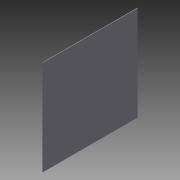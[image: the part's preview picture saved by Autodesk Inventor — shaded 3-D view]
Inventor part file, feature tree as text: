
AUTODESK INVENTOR PART (.ipt)
format: ipt  version: 2013 (Build 170138000, 138)  size: 72,704 bytes
history: native  units: in
note: dims shown in document units (in); Inventor stores cm internally (conversion verified against a paired STEP export)
features: sheet_metal_op x1, sketch x1, other x1
ambient origin geometry x8: Origin, YZ Plane, XZ Plane, XY Plane, X Axis, Y Axis, Z Axis, Center Point
bodies: Solid1 (feature_tree)
feature tree (3):
  sheet_metal_op  "Face1"
  sketch  "Sketch1"  dims[d0=24.0in d2=24.0in d3=0.12in]
  other  "Plate1"
